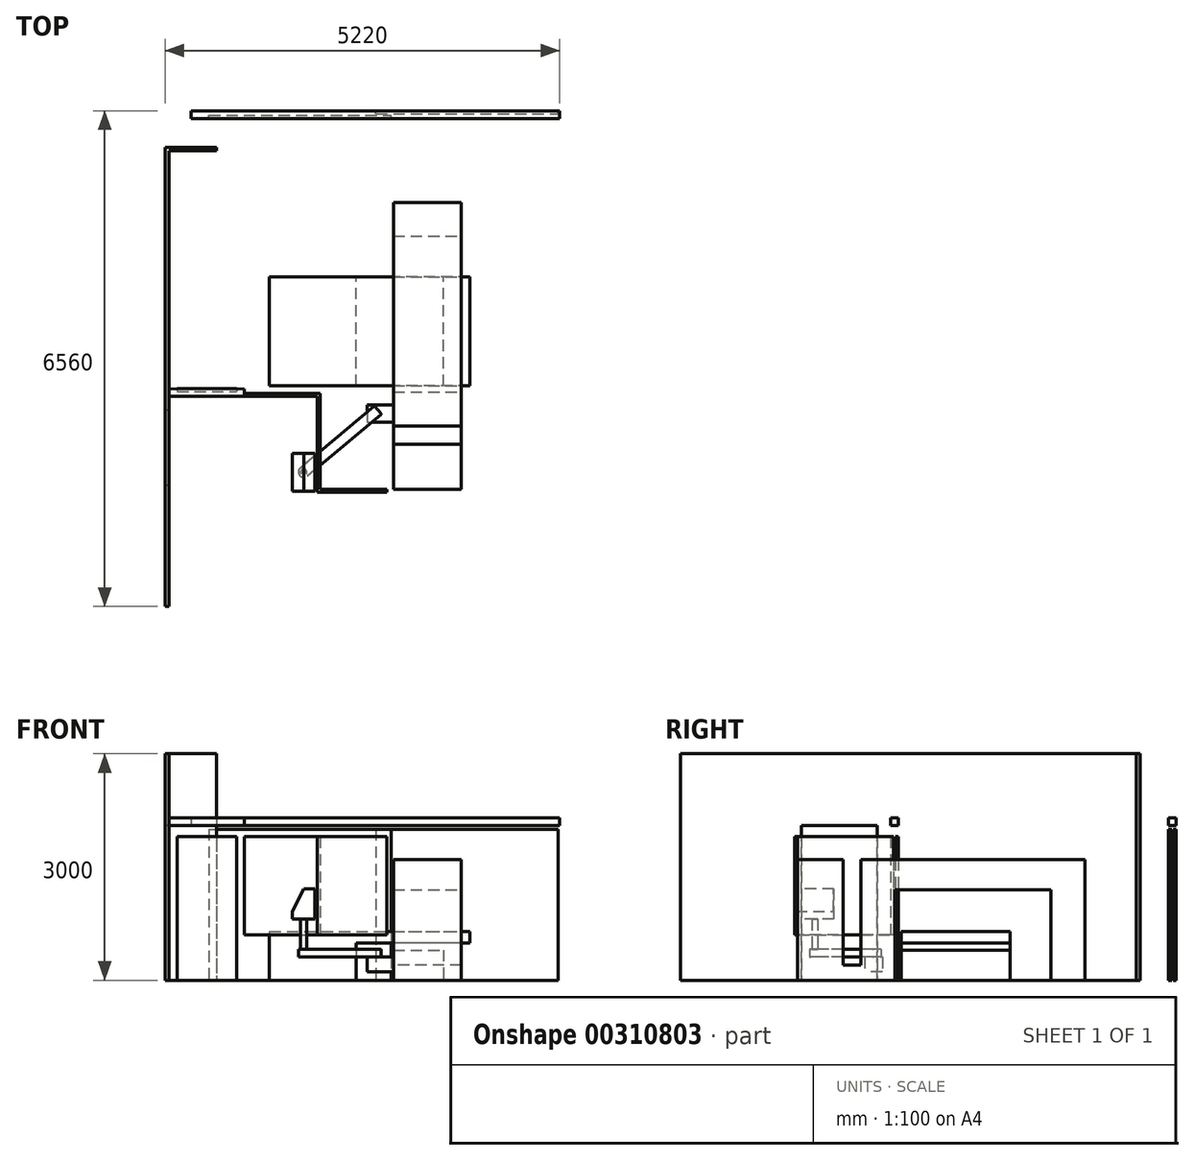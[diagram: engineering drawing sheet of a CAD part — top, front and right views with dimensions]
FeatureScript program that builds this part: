
annotation { "Feature Type Name" : "Feature", "Feature Type Description" : "" }
export const myFeature = defineFeature(function(context is Context, id is Id, definition is map)
    precondition{}
    {
        {
            var Q0;
            Q0=qCreatedBy(makeId("Top.planeOp"),FACE);
            var sketch = newSketch(context, id + "F0", { "sketchPlane" : qUnion([Q0])});
            skLineSegment(sketch, "E0.bottom", {"start": v(2610, 4000) * mm, "end": v(2810, 4000) * mm});
            skLineSegment(sketch, "E0.left", {"start": v(2610, 4000) * mm, "end": v(2610, -3000) * mm});
            skLineSegment(sketch, "E0.right", {"start": v(2810, 4000) * mm, "end": v(2810, -3000) * mm});
            skLineSegment(sketch, "E1", {"start": v(-98.37, 0) * mm, "end": v(165.03, 0) * mm, "construction": true});
            skLineSegment(sketch, "E2.left", {"start": v(-2560, -3000) * mm, "end": v(-2560, 3030) * mm});
            skLineSegment(sketch, "E2.right", {"start": v(-2610, -4000) * mm, "end": v(-2610, 3030) * mm});
            skLineSegment(sketch, "E3.bottom", {"start": v(2610, -3000) * mm, "end": v(-2610, -3000) * mm});
            skLineSegment(sketch, "E3.top", {"start": v(2810, -3200) * mm, "end": v(-2610, -3200) * mm});
            skLineSegment(sketch, "E3.left", {"start": v(2810, -3000) * mm, "end": v(2810, -3200) * mm});
            skLineSegment(sketch, "E3.right", {"start": v(-2610, -3000) * mm, "end": v(-2610, -3200) * mm});
            skLineSegment(sketch, "E4.bottom", {"start": v(-2560, 3030) * mm, "end": v(-1930, 3030) * mm});
            skLineSegment(sketch, "E4.top", {"start": v(-2610, 3080) * mm, "end": v(-1930, 3080) * mm});
            skLineSegment(sketch, "E4.left", {"start": v(-2610, 3030) * mm, "end": v(-2610, 3080) * mm});
            skLineSegment(sketch, "E4.right", {"start": v(-1930, 3030) * mm, "end": v(-1930, 3080) * mm});
            skLineSegment(sketch, "E5.bottom", {"start": v(-1230, -80) * mm, "end": v(1070, -80) * mm});
            skLineSegment(sketch, "E5.top", {"start": v(-1230, 1360) * mm, "end": v(1070, 1360) * mm});
            skLineSegment(sketch, "E5.left", {"start": v(-1230, -80) * mm, "end": v(-1230, 1360) * mm});
            skLineSegment(sketch, "E5.right", {"start": v(1070, -80) * mm, "end": v(1070, 1360) * mm});
            skLineSegment(sketch, "E6.bottom", {"start": v(410, -1450) * mm, "end": v(1310, -1450) * mm});
            skLineSegment(sketch, "E6.top", {"start": v(410, -160) * mm, "end": v(1310, -160) * mm});
            skLineSegment(sketch, "E6.left", {"start": v(410, -1450) * mm, "end": v(410, -160) * mm});
            skLineSegment(sketch, "E6.right", {"start": v(1310, -1450) * mm, "end": v(1310, -160) * mm});
            skLineSegment(sketch, "E7.bottom", {"start": v(410, 1900) * mm, "end": v(1310, 1900) * mm});
            skLineSegment(sketch, "E7.top", {"start": v(410, 2350) * mm, "end": v(1310, 2350) * mm});
            skLineSegment(sketch, "E7.left", {"start": v(410, 1900) * mm, "end": v(410, 2350) * mm});
            skLineSegment(sketch, "E7.right", {"start": v(1310, 1900) * mm, "end": v(1310, 2350) * mm});
            skLineSegment(sketch, "E8", {"start": v(1070, 640) * mm, "end": v(-1230, 640) * mm, "construction": true});
            skLineSegment(sketch, "E9", {"start": v(-80, -80) * mm, "end": v(-80, 1360) * mm});
            skLineSegment(sketch, "E10.bottom", {"start": v(1310, -160) * mm, "end": v(410, -160) * mm});
            skLineSegment(sketch, "E10.top", {"start": v(1310, 1900) * mm, "end": v(410, 1900) * mm});
            skLineSegment(sketch, "E10.left", {"start": v(1310, -160) * mm, "end": v(1310, 1900) * mm});
            skLineSegment(sketch, "E10.right", {"start": v(410, -160) * mm, "end": v(410, 1900) * mm});
            skSolve(sketch);
        }
        {
            var Q0;
            {var subQ1=sQuery(id+"F0.wireOp",EDGE,"E2.left");Q0=makeQuery(id+"F0.imprint","IMPRINT",FACE,{"disambiguationData":[TD([[makeQuery(id+"F0.imprint","IMPRINT",EDGE,{"derivedFrom":subQ1}),1.0]])]});}
            extrude(context, id + "F1", {"entities" : qUnion([Q0]), "depth" : 3000 * mm});
        }
        {
            var Q0;
            {var subQ0=sQuery(id+"F0.wireOp",EDGE,"E5.left");Q0=makeQuery(id+"F0.imprint","IMPRINT",FACE,{"disambiguationData":[TD([[makeQuery(id+"F0.imprint","IMPRINT",EDGE,{"derivedFrom":subQ0}),-1.0]])]});}
            extrude(context, id + "F2", {"entities" : qUnion([Q0]), "depth" : 645 * mm});
        }
        {
            var Q0;
            Q0=makeQuery(id+"F0.imprint","IMPRINT",FACE,{"disambiguationData":[TD([[makeQuery(id+"F0.imprint","IMPRINT",EDGE,{"derivedFrom":sQuery(id+"F0.wireOp",EDGE,"E7.top")}),-1.0]])]});
            var Q1;
            {var subQ5=sQuery(id+"F0.wireOp",EDGE,"E10.top");Q1=makeQuery(id+"F0.imprint","IMPRINT",FACE,{"disambiguationData":[TD([[makeQuery(id+"F0.imprint","IMPRINT",EDGE,{"derivedFrom":subQ5}),1.0]])]});}
            var Q2;
            {var subQ0=sQuery(id+"F0.wireOp",EDGE,"E10.right");var subQ1=sQuery(id+"F0.wireOp",EDGE,"E5.bottom");var subQ2=makeQuery(id+"F0.imprint","INTERSECT",VERTEX,{"derivedFrom":[subQ1,subQ0]});Q2=makeQuery(id+"F0.imprint","IMPRINT",FACE,{"disambiguationData":[TD([[makeQuery(id+"F0.imprint","IMPRINT",EDGE,{"disambiguationData":[TD([[subQ2,-1.0]])],"derivedFrom":subQ1}),1.0]])]});}
            var Q3;
            {var subQ5=sQuery(id+"F0.wireOp",EDGE,"E10.bottom");Q3=makeQuery(id+"F0.imprint","IMPRINT",FACE,{"disambiguationData":[TD([[makeQuery(id+"F0.imprint","IMPRINT",EDGE,{"derivedFrom":subQ5}),-1.0]])]});}
            var Q4;
            Q4=makeQuery(id+"F0.imprint","IMPRINT",FACE,{"disambiguationData":[TD([[makeQuery(id+"F0.imprint","IMPRINT",EDGE,{"derivedFrom":sQuery(id+"F0.wireOp",EDGE,"E6.bottom")}),1.0]])]});
            extrude(context, id + "F3", {"entities" : qUnion([Q0, Q1, Q2, Q3, Q4]), "depth" : 400 * mm});
        }
        {
            var Q0;
            Q0=makeQuery(id+"F0.imprint","IMPRINT",FACE,{"disambiguationData":[TD([[makeQuery(id+"F0.imprint","IMPRINT",EDGE,{"derivedFrom":sQuery(id+"F0.wireOp",EDGE,"E7.top")}),-1.0]])]});
            var Q1;
            Q1=makeQuery(id+"F0.imprint","IMPRINT",FACE,{"disambiguationData":[TD([[makeQuery(id+"F0.imprint","IMPRINT",EDGE,{"derivedFrom":sQuery(id+"F0.wireOp",EDGE,"E6.bottom")}),1.0]])]});
            extrude(context, id + "F4", {"entities" : qUnion([Q0, Q1]), "operationType" : NewBodyOperationType.ADD, "depth" : 1600 * mm});
        }
        {
            var Q0;
            Q0=makeQuery(id+"F4.opExtrude","CAP_FACE",FACE,{"disambiguationData":[OSD([sQuery(id+"F0.wireOp",EDGE,"E7.top"),sQuery(id+"F0.wireOp",EDGE,"E7.left"),sQuery(id+"F0.wireOp",EDGE,"E7.right"),sQuery(id+"F0.wireOp",EDGE,"E10.top")])],"isStart":false});
            var sketch = newSketch(context, id + "F5", { "sketchPlane" : qUnion([Q0])});
            skLineSegment(sketch, "E11.0", {"start": v(410, 2350) * mm, "end": v(1310, 2350) * mm, "construction": true});
            skLineSegment(sketch, "E12.0", {"start": v(410, -1450) * mm, "end": v(1310, -1450) * mm, "construction": true});
            skLineSegment(sketch, "E13.bottom", {"start": v(410, 2350) * mm, "end": v(1310, 2350) * mm});
            skLineSegment(sketch, "E13.top", {"start": v(410, -1450) * mm, "end": v(1310, -1450) * mm});
            skLineSegment(sketch, "E13.left", {"start": v(410, 2350) * mm, "end": v(410, -1450) * mm});
            skLineSegment(sketch, "E13.right", {"start": v(1310, 2350) * mm, "end": v(1310, -1450) * mm});
            skLineSegment(sketch, "E14", {"start": v(1310, -850) * mm, "end": v(410, -850) * mm});
            skLineSegment(sketch, "E15", {"start": v(1310, -610) * mm, "end": v(410, -610) * mm});
            skSolve(sketch);
        }
        {
            var Q0;
            Q0 = qSketchRegion(id + "F5", true);
            extrude(context, id + "F6", {"entities" : qUnion([Q0]), "operationType" : NewBodyOperationType.ADD, "oppositeDirection" : true, "depth" : 400 * mm});
        }
        {
            var Q0;
            Q0=makeQuery(id+"F2.opExtrude","SWEPT_FACE",FACE,{"disambiguationData":[OSD([sQuery(id+"F0.wireOp",EDGE,"E9")])]});
            var sketch = newSketch(context, id + "F7", { "sketchPlane" : qUnion([Q0])});
            skLineSegment(sketch, "E16.bottom", {"start": v(-80, 645) * mm, "end": v(1360, 645) * mm});
            skLineSegment(sketch, "E16.top", {"start": v(-80, 495) * mm, "end": v(1360, 495) * mm});
            skLineSegment(sketch, "E16.left", {"start": v(-80, 645) * mm, "end": v(-80, 495) * mm});
            skLineSegment(sketch, "E16.right", {"start": v(1360, 645) * mm, "end": v(1360, 495) * mm});
            skSolve(sketch);
        }
        {
            var Q0;
            Q0 = qSketchRegion(id + "F7", true);
            extrude(context, id + "F8", {"entities" : qUnion([Q0]), "operationType" : NewBodyOperationType.ADD, "depth" : 1500 * mm});
        }
        {
            var Q0;
            {var subQ0=sQuery(id+"F5.wireOp",EDGE,"E14");Q0=makeQuery(id+"F5.imprint","IMPRINT",FACE,{"disambiguationData":[TD([[makeQuery(id+"F5.imprint","IMPRINT",EDGE,{"derivedFrom":subQ0}),-1.0]])]});}
            extrude(context, id + "F9", {"entities" : qUnion([Q0]), "operationType" : NewBodyOperationType.REMOVE, "oppositeDirection" : true, "depth" : 1400 * mm});
        }
        {
            var Q0;
            Q0=makeQuery(id+"F1.opExtrude","SWEPT_FACE",FACE,{"disambiguationData":[OSD([sQuery(id+"F0.wireOp",EDGE,"E2.right"),sQuery(id+"F0.wireOp",EDGE,"E4.left")])]});
            var sketch = newSketch(context, id + "F10", { "sketchPlane" : qUnion([Q0])});
            skLineSegment(sketch, "E17.bottom", {"start": v(1400, 0) * mm, "end": v(400, 0) * mm});
            skLineSegment(sketch, "E17.top", {"start": v(1400, 2050) * mm, "end": v(400, 2050) * mm});
            skLineSegment(sketch, "E17.left", {"start": v(1400, 0) * mm, "end": v(1400, 2050) * mm});
            skLineSegment(sketch, "E17.right", {"start": v(400, 0) * mm, "end": v(400, 2050) * mm});
            skSolve(sketch);
        }
        {
            var Q0;
            Q0 = qSketchRegion(id + "F10", true);
            extrude(context, id + "F11", {"entities" : qUnion([Q0]), "operationType" : NewBodyOperationType.REMOVE, "endBound" : BoundingType.UP_TO_NEXT, "oppositeDirection" : true, "depth" : 25 * mm});
        }
        {
            var Q0;
            {var subQ0=sQuery(id+"F0.wireOp",EDGE,"E7.left");var subQ1=sQuery(id+"F0.wireOp",EDGE,"E6.left");Q0=makeQuery(id+"F6.boolean.opBoolean","MERGE",FACE,{"derivedFrom":[makeQuery(id+"F4.boolean.opBoolean","MERGE",FACE,{"derivedFrom":[makeQuery(id+"F3.opExtrude","SWEPT_FACE",FACE,{"disambiguationData":[OSD([subQ1,subQ0,sQuery(id+"F0.wireOp",EDGE,"E10.right")])]}),makeQuery(id+"F4.opExtrude","SWEPT_FACE",FACE,{"disambiguationData":[OSD([subQ1])]}),makeQuery(id+"F4.opExtrude","SWEPT_FACE",FACE,{"disambiguationData":[OSD([subQ0])]})]}),makeQuery(id+"F6.opExtrude","SWEPT_FACE",FACE,{"disambiguationData":[OSD([sQuery(id+"F5.wireOp",EDGE,"E13.left")])]})]});}
            var sketch = newSketch(context, id + "F12", { "sketchPlane" : qUnion([Q0])});
            skLineSegment(sketch, "E18.bottom", {"start": v(330, 308.87) * mm, "end": v(560, 308.87) * mm});
            skLineSegment(sketch, "E18.top", {"start": v(330, 108.87) * mm, "end": v(560, 108.87) * mm});
            skLineSegment(sketch, "E18.left", {"start": v(330, 308.87) * mm, "end": v(330, 108.87) * mm});
            skLineSegment(sketch, "E18.right", {"start": v(560, 308.87) * mm, "end": v(560, 108.87) * mm});
            skSolve(sketch);
        }
        {
            var Q0;
            Q0 = qSketchRegion(id + "F12", true);
            extrude(context, id + "F13", {"entities" : qUnion([Q0]), "operationType" : NewBodyOperationType.ADD, "depth" : 350 * mm});
        }
        {
            var Q0;
            Q0=makeQuery(id+"F13.opExtrude","SWEPT_FACE",FACE,{"disambiguationData":[OSD([sQuery(id+"F12.wireOp",EDGE,"E18.bottom")])]});
            var sketch = newSketch(context, id + "F14", { "sketchPlane" : qUnion([Q0])});
            skCircle(sketch, "E19", {"center": v(150, -445) * mm, "radius": 70 * mm, "construction": true});
            skPoint(sketch, "E19.centerSnap0", {"position": v(410, -445) * mm});
            skLineSegment(sketch, "E20", {"start": v(161.84, -350.21) * mm, "end": v(245.4, -449.8) * mm});
            skLineSegment(sketch, "E21", {"start": v(150, -445) * mm, "end": v(203.62, -400) * mm, "construction": true});
            skLineSegment(sketch, "E22", {"start": v(154.8, -349.6) * mm, "end": v(-821.9, -1169.15) * mm});
            skLineSegment(sketch, "E23", {"start": v(244.79, -456.84) * mm, "end": v(-731.92, -1276.4) * mm});
            skArc(sketch, "E24", {"start": v(-821.9, -1169.15) * mm, "mid": v(-830.54, -1267.77) * mm, "end": v(-731.92, -1276.4) * mm});
            skPoint(sketch, "E25.visualSharp", {"position": v(158.63, -346.38) * mm});
            skArc(sketch, "E25.filletArc", {"start": v(161.84, -350.21) * mm, "mid": v(158.45, -348.44) * mm, "end": v(154.8, -349.6) * mm});
            skPoint(sketch, "E26.visualSharp", {"position": v(248.62, -453.63) * mm});
            skArc(sketch, "E26.filletArc", {"start": v(244.79, -456.84) * mm, "mid": v(246.56, -453.45) * mm, "end": v(245.4, -449.8) * mm});
            skSolve(sketch);
        }
        {
            var Q0;
            Q0 = qSketchRegion(id + "F14", true);
            extrude(context, id + "F15", {"entities" : qUnion([Q0]), "depth" : 100 * mm});
        }
        {
            var Q0;
            Q0=makeQuery(id+"F15.opExtrude","CAP_FACE",FACE,{"disambiguationData":[OSD([sQuery(id+"F14.wireOp",EDGE,"E20"),sQuery(id+"F14.wireOp",EDGE,"E22"),sQuery(id+"F14.wireOp",EDGE,"E23"),sQuery(id+"F14.wireOp",EDGE,"E24"),sQuery(id+"F14.wireOp",EDGE,"E25.filletArc"),sQuery(id+"F14.wireOp",EDGE,"E26.filletArc")])],"isStart":false});
            var sketch = newSketch(context, id + "F16", { "sketchPlane" : qUnion([Q0])});
            skCircle(sketch, "E27", {"center": v(-776.91, -1222.77) * mm, "radius": 40 * mm});
            skSolve(sketch);
        }
        {
            var Q0;
            Q0 = qSketchRegion(id + "F16", true);
            extrude(context, id + "F17", {"entities" : qUnion([Q0]), "operationType" : NewBodyOperationType.ADD, "depth" : 400 * mm});
        }
        {
            var Q0;
            Q0=makeQuery(id+"F17.opExtrude","CAP_FACE",FACE,{"disambiguationData":[OSD([sQuery(id+"F16.wireOp",EDGE,"E27")])],"isStart":false});
            var sketch = newSketch(context, id + "F18", { "sketchPlane" : qUnion([Q0])});
            skLineSegment(sketch, "E28.bottom", {"start": v(-926.91, -972.77) * mm, "end": v(-626.91, -972.77) * mm});
            skLineSegment(sketch, "E28.top", {"start": v(-926.91, -1472.77) * mm, "end": v(-626.91, -1472.77) * mm});
            skLineSegment(sketch, "E28.left", {"start": v(-926.91, -972.77) * mm, "end": v(-926.91, -1472.77) * mm});
            skLineSegment(sketch, "E28.right", {"start": v(-626.91, -972.77) * mm, "end": v(-626.91, -1472.77) * mm});
            skPoint(sketch, "E28.middle", {"position": v(-776.91, -1222.77) * mm});
            skSolve(sketch);
        }
        {
            var Q0;
            Q0 = qSketchRegion(id + "F18", true);
            extrude(context, id + "F19", {"entities" : qUnion([Q0]), "depth" : 400 * mm});
        }
        {
            var Q0;
            Q0=makeQuery(id+"F19.opExtrude","CAP_EDGE",EDGE,{"disambiguationData":[OSD([sQuery(id+"F18.wireOp",EDGE,"E28.left")])],"isStart":false});
            chamfer(context, id + "F20", {"entities" : qUnion([Q0]), "chamferType" : ChamferType.TWO_OFFSETS, "width1" : 150 * mm, "oppositeDirection" : false, "width2" : 300 * mm, "tangentPropagation" : true});
        }
        {
            var Q0;
            Q0=qCreatedBy(makeId("Top.planeOp"),FACE);
            cPlane(context, id + "F21", {"entities" : qUnion([Q0]), "cplaneType" : CPlaneType.OFFSET, "offset" : 600 * mm, "width" : 150 * mm, "height" : 150 * mm});
        }
        {
            var Q0;
            Q0=qCreatedBy(id+"F21.planeOp",FACE);
            var sketch = newSketch(context, id + "F22", { "sketchPlane" : qUnion([Q0])});
            skLineSegment(sketch, "E29.0", {"start": v(410, -1450) * mm, "end": v(410, -160) * mm, "construction": true});
            skLineSegment(sketch, "E30.0", {"start": v(-1230, -80) * mm, "end": v(1070, -80) * mm, "construction": true});
            skLineSegment(sketch, "E31", {"start": v(324.48, -1450) * mm, "end": v(-560, -1450) * mm});
            skLineSegment(sketch, "E32", {"start": v(-560, -1450) * mm, "end": v(-560, -180) * mm});
            skLineSegment(sketch, "E33", {"start": v(-560, -180) * mm, "end": v(-1560, -180) * mm});
            skLineSegment(sketch, "E34", {"start": v(-1560, -220) * mm, "end": v(-600, -220) * mm});
            skLineSegment(sketch, "E35", {"start": v(-600, -220) * mm, "end": v(-600, -1490) * mm});
            skLineSegment(sketch, "E36", {"start": v(-600, -1490) * mm, "end": v(324.48, -1490) * mm});
            skLineSegment(sketch, "E37", {"start": v(324.48, -1490) * mm, "end": v(324.48, -1450) * mm});
            skLineSegment(sketch, "E38", {"start": v(-1560, -180) * mm, "end": v(-1560, -220) * mm});
            skSolve(sketch);
        }
        {
            var Q0;
            Q0 = qSketchRegion(id + "F22", true);
            extrude(context, id + "F23", {"entities" : qUnion([Q0]), "depth" : 1300 * mm});
        }
        {
            var Q0;
            Q0=qCreatedBy(makeId("Top.planeOp"),FACE);
            var sketch = newSketch(context, id + "F24", { "sketchPlane" : qUnion([Q0])});
            skPoint(sketch, "E39.0", {"position": v(-1560, -220) * mm});
            skLineSegment(sketch, "E40.bottom", {"start": v(-1560, -220) * mm, "end": v(-1660, -220) * mm});
            skLineSegment(sketch, "E40.top", {"start": v(-1560, -120) * mm, "end": v(-1660, -120) * mm});
            skLineSegment(sketch, "E40.left", {"start": v(-1560, -220) * mm, "end": v(-1560, -120) * mm});
            skLineSegment(sketch, "E40.right", {"start": v(-1660, -220) * mm, "end": v(-1660, -120) * mm});
            skLineSegment(sketch, "E41", {"start": v(-1560, -220) * mm, "end": v(-1660, -120) * mm, "construction": true});
            skLineSegment(sketch, "E42.bottom", {"start": v(-1657, -217) * mm, "end": v(-1563, -217) * mm});
            skLineSegment(sketch, "E42.top", {"start": v(-1657, -123) * mm, "end": v(-1563, -123) * mm});
            skLineSegment(sketch, "E42.left", {"start": v(-1657, -217) * mm, "end": v(-1657, -123) * mm});
            skLineSegment(sketch, "E42.right", {"start": v(-1563, -217) * mm, "end": v(-1563, -123) * mm});
            skPoint(sketch, "E42.middle", {"position": v(-1610, -170) * mm});
            skLineSegment(sketch, "E43.0", {"start": v(-2560, -3000) * mm, "end": v(-2560, 3030) * mm, "construction": true});
            skLineSegment(sketch, "E44.bottom", {"start": v(-2560, -217) * mm, "end": v(-2460, -217) * mm});
            skLineSegment(sketch, "E44.top", {"start": v(-2560, -117) * mm, "end": v(-2460, -117) * mm});
            skLineSegment(sketch, "E44.left", {"start": v(-2560, -217) * mm, "end": v(-2560, -117) * mm});
            skLineSegment(sketch, "E44.right", {"start": v(-2460, -217) * mm, "end": v(-2460, -117) * mm});
            skLineSegment(sketch, "E45.bottom", {"start": v(-2030, 3460) * mm, "end": v(380, 3460) * mm});
            skLineSegment(sketch, "E45.top", {"start": v(-2030, 3500) * mm, "end": v(380, 3500) * mm});
            skLineSegment(sketch, "E45.left", {"start": v(-2030, 3460) * mm, "end": v(-2030, 3500) * mm});
            skLineSegment(sketch, "E45.right", {"start": v(380, 3460) * mm, "end": v(380, 3500) * mm});
            skLineSegment(sketch, "E46.bottom", {"start": v(180, 3520) * mm, "end": v(2590, 3520) * mm});
            skLineSegment(sketch, "E46.top", {"start": v(180, 3560) * mm, "end": v(2590, 3560) * mm});
            skLineSegment(sketch, "E46.left", {"start": v(180, 3520) * mm, "end": v(180, 3560) * mm});
            skLineSegment(sketch, "E46.right", {"start": v(2590, 3520) * mm, "end": v(2590, 3560) * mm});
            skLineSegment(sketch, "E47.bottom", {"start": v(-2168.56, 3460) * mm, "end": v(-2268.56, 3460) * mm});
            skLineSegment(sketch, "E47.top", {"start": v(-2168.56, 3560) * mm, "end": v(-2268.56, 3560) * mm});
            skLineSegment(sketch, "E47.left", {"start": v(-2168.56, 3460) * mm, "end": v(-2168.56, 3560) * mm});
            skLineSegment(sketch, "E47.right", {"start": v(-2268.56, 3460) * mm, "end": v(-2268.56, 3560) * mm});
            skPoint(sketch, "E48.oppositeSnap0", {"position": v(-2560, -167) * mm});
            skLineSegment(sketch, "E48.bottom", {"start": v(-2450, -117) * mm, "end": v(-1667, -117) * mm});
            skLineSegment(sketch, "E48.top", {"start": v(-2450, -157) * mm, "end": v(-1667, -157) * mm});
            skLineSegment(sketch, "E48.left", {"start": v(-2450, -117) * mm, "end": v(-2450, -157) * mm});
            skLineSegment(sketch, "E48.right", {"start": v(-1667, -117) * mm, "end": v(-1667, -157) * mm});
            skLineSegment(sketch, "E49.bottom", {"start": v(-2268.56, 3460) * mm, "end": v(-2228.56, 3460) * mm});
            skLineSegment(sketch, "E49.top", {"start": v(-2268.56, 3080) * mm, "end": v(-2228.56, 3080) * mm});
            skLineSegment(sketch, "E49.left", {"start": v(-2268.56, 3460) * mm, "end": v(-2268.56, 3080) * mm});
            skLineSegment(sketch, "E49.right", {"start": v(-2228.56, 3460) * mm, "end": v(-2228.56, 3080) * mm});
            skSolve(sketch);
        }
        {
            var Q0;
            Q0=sQuery(id+"F24.wireOp",EDGE,"E47.left");
            var Q1;
            Q1=sQuery(id+"F24.wireOp",EDGE,"E47.top");
            var Q2;
            Q2=sQuery(id+"F24.wireOp",EDGE,"E47.right");
            var Q3;
            Q3=sQuery(id+"F24.wireOp",EDGE,"E47.bottom");
            var Q4;
            Q4=sQuery(id+"F24.wireOp",EDGE,"E44.bottom");
            var Q5;
            Q5=sQuery(id+"F24.wireOp",EDGE,"E44.right");
            var Q6;
            Q6=sQuery(id+"F24.wireOp",EDGE,"E44.top");
            var Q7;
            Q7=sQuery(id+"F24.wireOp",EDGE,"E44.left");
            var Q8;
            Q8=sQuery(id+"F24.wireOp",EDGE,"E40.left");
            var Q9;
            Q9=sQuery(id+"F24.wireOp",EDGE,"E40.bottom");
            var Q10;
            Q10=sQuery(id+"F24.wireOp",EDGE,"E42.bottom");
            var Q11;
            Q11=sQuery(id+"F24.wireOp",EDGE,"E42.right");
            var Q12;
            Q12=sQuery(id+"F24.wireOp",EDGE,"E40.top");
            var Q13;
            Q13=sQuery(id+"F24.wireOp",EDGE,"E42.top");
            var Q14;
            Q14=sQuery(id+"F24.wireOp",EDGE,"E40.right");
            var Q15;
            Q15=sQuery(id+"F24.wireOp",EDGE,"E42.left");
            extrude(context, id + "F25", {"bodyType" : ToolBodyType.SURFACE, "surfaceEntities" : qUnion([Q0, Q1, Q2, Q3, Q4, Q5, Q6, Q7, Q8, Q9, Q10, Q11, Q12, Q13, Q14, Q15]), "depth" : 2150 * mm});
        }
        {
            var Q0;
            Q0=makeQuery(id+"F24.imprint","IMPRINT",FACE,{"disambiguationData":[TD([[makeQuery(id+"F24.imprint","IMPRINT",EDGE,{"derivedFrom":sQuery(id+"F24.wireOp",EDGE,"E45.bottom")}),1.0]])]});
            var Q1;
            Q1=makeQuery(id+"F24.imprint","IMPRINT",FACE,{"disambiguationData":[TD([[makeQuery(id+"F24.imprint","IMPRINT",EDGE,{"derivedFrom":sQuery(id+"F24.wireOp",EDGE,"E46.bottom")}),1.0]])]});
            extrude(context, id + "F26", {"entities" : qUnion([Q0, Q1]), "depth" : 2000 * mm});
        }
        {
            var Q0;
            Q0=qCreatedBy(makeId("Top.planeOp"),FACE);
            cPlane(context, id + "F27", {"entities" : qUnion([Q0]), "cplaneType" : CPlaneType.OFFSET, "offset" : 2050 * mm, "width" : 150 * mm, "height" : 150 * mm});
        }
        {
            var Q0;
            Q0=qCreatedBy(id+"F27.planeOp",FACE);
            var sketch = newSketch(context, id + "F28", { "sketchPlane" : qUnion([Q0])});
            skLineSegment(sketch, "E50.0", {"start": v(-1560, -120) * mm, "end": v(-1560, -220) * mm});
            skLineSegment(sketch, "E50.1", {"start": v(-2560, -117) * mm, "end": v(-2560, -217) * mm});
            skLineSegment(sketch, "E51.0", {"start": v(-2268.56, 3560) * mm, "end": v(-2268.56, 3460) * mm});
            skLineSegment(sketch, "E52", {"start": v(-2268.56, 3560) * mm, "end": v(2610, 3560) * mm});
            skLineSegment(sketch, "E53", {"start": v(-2268.56, 3460) * mm, "end": v(2610, 3460) * mm});
            skLineSegment(sketch, "E54.0", {"start": v(2610, 3560) * mm, "end": v(2610, 3460) * mm});
            skPoint(sketch, "E55.orphan", {"position": v(2610, -3000) * mm});
            skPoint(sketch, "E56.orphan", {"position": v(2610, 4000) * mm});
            skLineSegment(sketch, "E57", {"start": v(-1560, -120) * mm, "end": v(-2560, -117) * mm});
            skLineSegment(sketch, "E58", {"start": v(-1560, -220) * mm, "end": v(-2560, -217) * mm});
            skSolve(sketch);
        }
        {
            var Q0;
            Q0 = qSketchRegion(id + "F28", true);
            extrude(context, id + "F29", {"entities" : qUnion([Q0]), "operationType" : NewBodyOperationType.ADD, "depth" : 100 * mm});
        }
        {
            var Q0;
            Q0=makeQuery(id+"F24.imprint","IMPRINT",FACE,{"disambiguationData":[TD([[makeQuery(id+"F24.imprint","IMPRINT",EDGE,{"derivedFrom":sQuery(id+"F24.wireOp",EDGE,"E49.bottom")}),-1.0]])]});
            var Q1;
            Q1=makeQuery(id+"F24.imprint","IMPRINT",FACE,{"disambiguationData":[TD([[makeQuery(id+"F24.imprint","IMPRINT",EDGE,{"derivedFrom":sQuery(id+"F24.wireOp",EDGE,"E48.bottom")}),-1.0]])]});
            extrude(context, id + "F30", {"entities" : qUnion([Q0, Q1]), "operationType" : NewBodyOperationType.ADD, "depth" : 1900 * mm});
        }
    });
